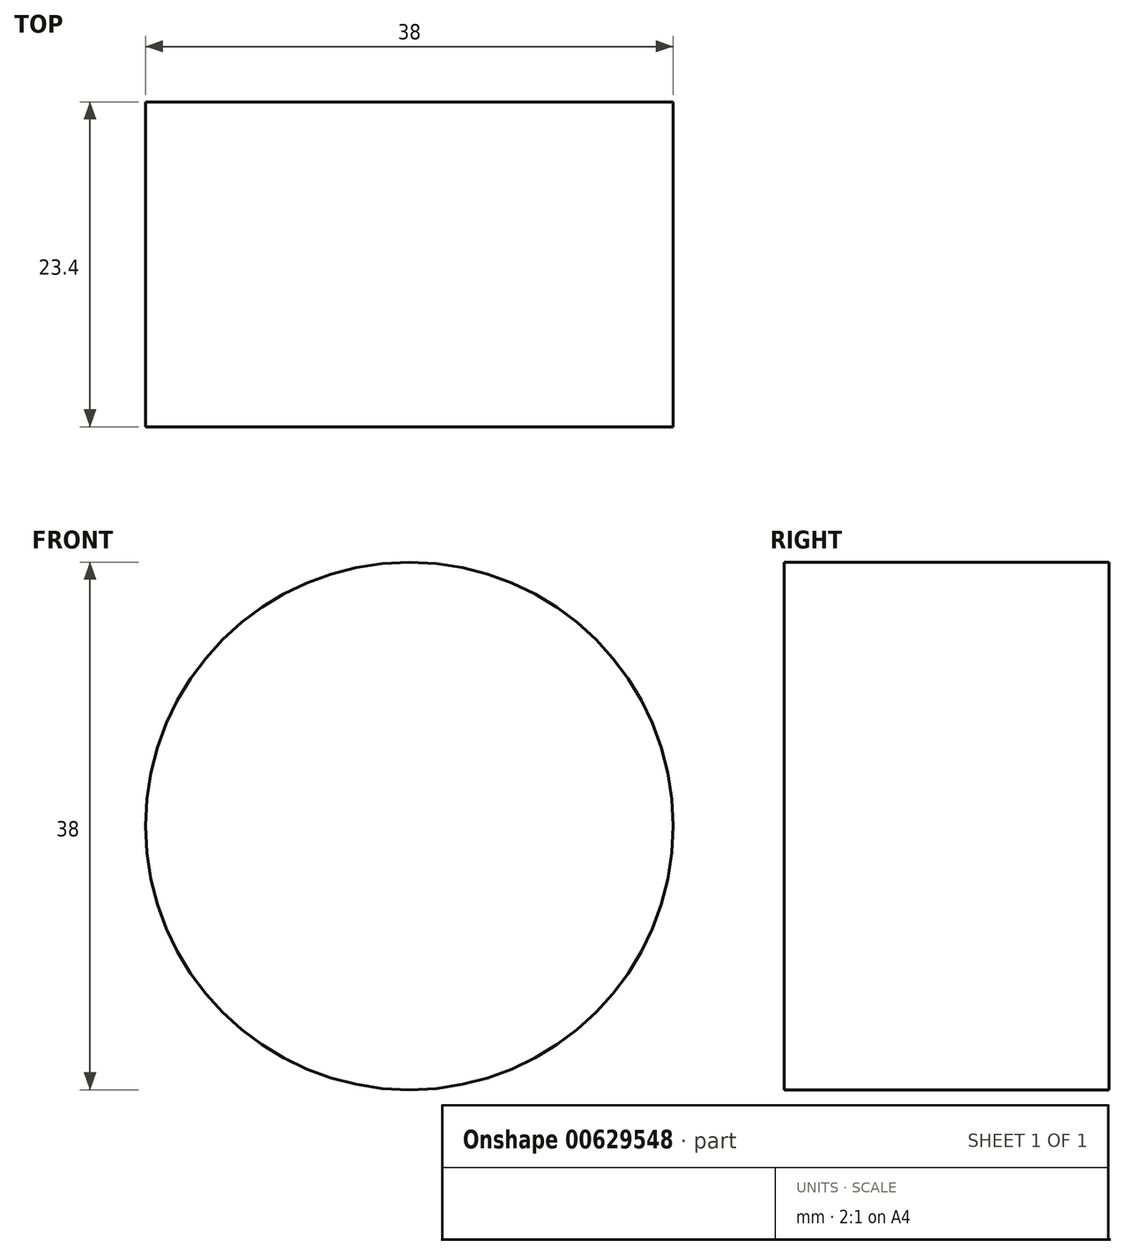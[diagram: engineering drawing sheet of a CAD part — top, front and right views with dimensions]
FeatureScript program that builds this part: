
annotation { "Feature Type Name" : "Feature", "Feature Type Description" : "" }
export const myFeature = defineFeature(function(context is Context, id is Id, definition is map)
    precondition{}
    {
        {
            var Q0;
            Q0=qCreatedBy(makeId("Front.planeOp"),FACE);
            var sketch = newSketch(context, id + "F0", { "sketchPlane" : qUnion([Q0])});
            skCircle(sketch, "E0", {"center": v(0, 0) * mm, "radius": 19 * mm});
            skSolve(sketch);
        }
        {
            var Q0;
            Q0=makeQuery(id+"F0.imprint","IMPRINT",FACE,{"disambiguationData":[TD([[makeQuery(id+"F0.imprint","IMPRINT",EDGE,{"derivedFrom":sQuery(id+"F0.wireOp",EDGE,"E0")}),1.0]])]});
            var Q1;
            Q1=sQuery(id+"F0.wireOp",EDGE,"E0");
            extrude(context, id + "F1", {"entities" : qUnion([Q0]), "surfaceEntities" : qUnion([Q1]), "depth" : 11.7 * mm, "offsetDistance" : 25 * mm, "hasSecondDirection" : true, "secondDirectionOppositeDirection" : true, "secondDirectionDepth" : 11.7 * mm});
        }
    });
